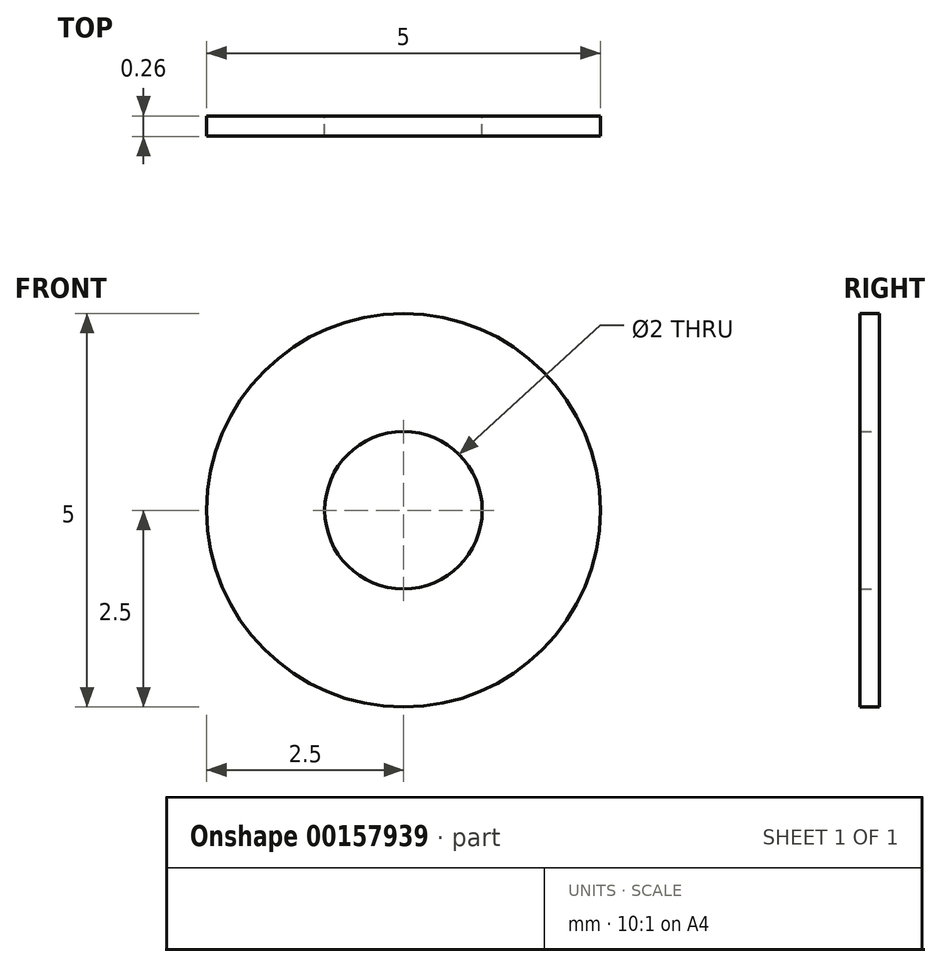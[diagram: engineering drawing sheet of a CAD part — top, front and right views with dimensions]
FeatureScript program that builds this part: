
annotation { "Feature Type Name" : "Feature", "Feature Type Description" : "" }
export const myFeature = defineFeature(function(context is Context, id is Id, definition is map)
    precondition{}
    {
        {
            assignVariable(context, id + "F0", {"name" : "h", "anyValue" : 0.25});
        }
        {
            var Q0;
            Q0=qCreatedBy(makeId("Front.planeOp"),FACE);
            var sketch = newSketch(context, id + "F1", { "sketchPlane" : qUnion([Q0])});
            skCircle(sketch, "E0", {"center": v(0, 0) * mm, "radius": 2.5 * mm});
            skCircle(sketch, "E1", {"center": v(0, 0) * mm, "radius": 1 * mm});
            skSolve(sketch);
        }
        {
            var Q0;
            Q0=makeQuery(id+"F1.imprint","IMPRINT",FACE,{"disambiguationData":[TD([[makeQuery(id+"F1.imprint","IMPRINT",EDGE,{"derivedFrom":sQuery(id+"F1.wireOp",EDGE,"E0")}),1.0]])]});
            extrude(context, id + "F2", {"entities" : qUnion([Q0]), "endBound" : BoundingType.SYMMETRIC, "depth" : (getVariable(context, 'h')) * mm});
        }
    });
